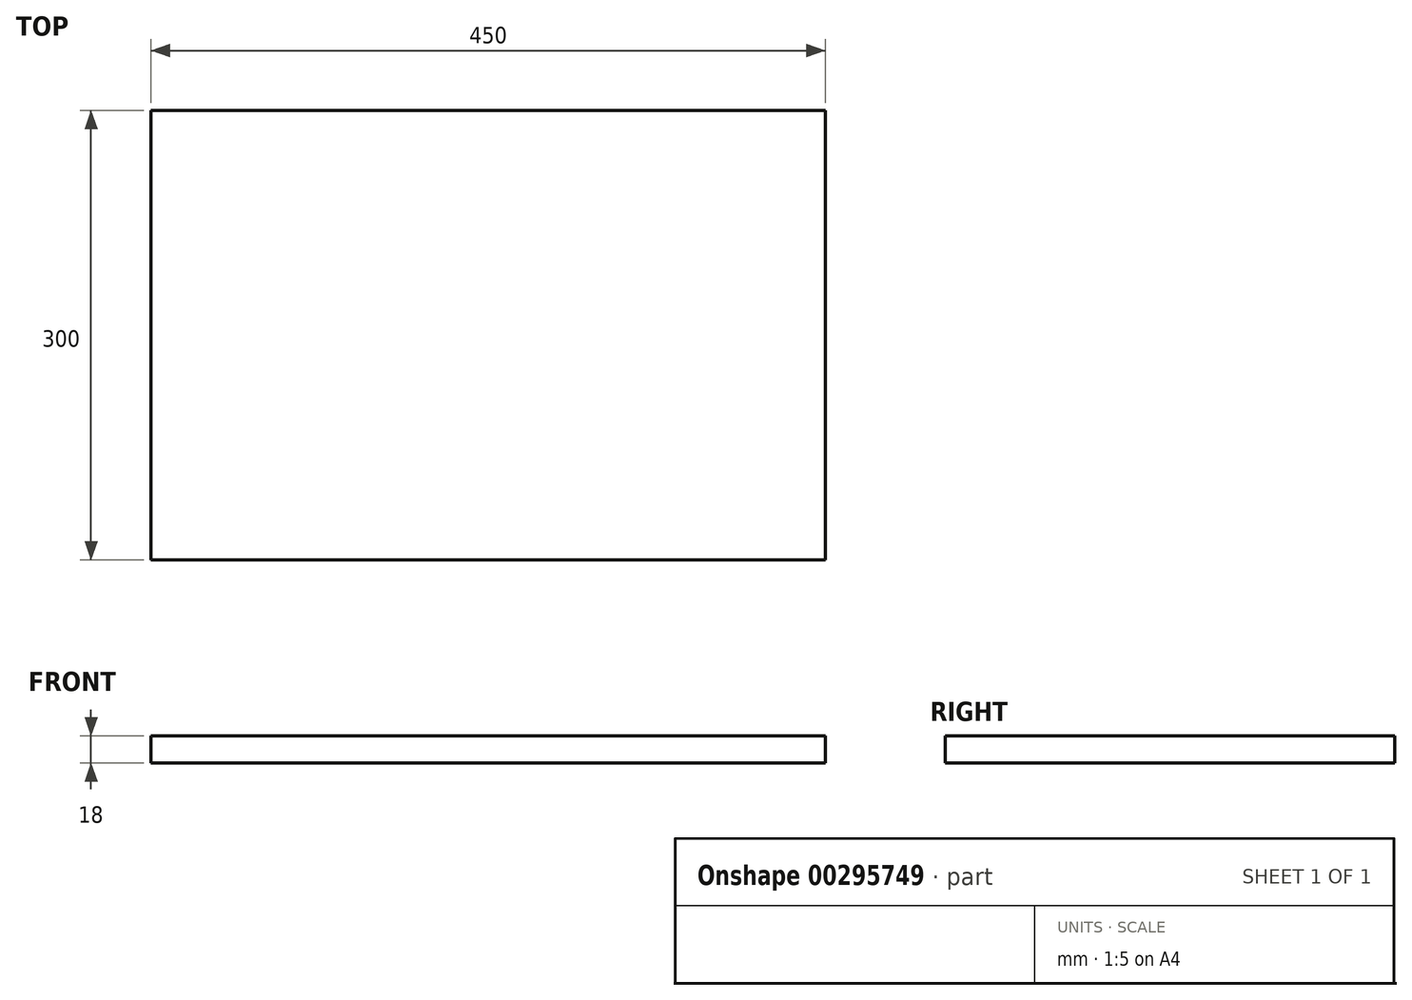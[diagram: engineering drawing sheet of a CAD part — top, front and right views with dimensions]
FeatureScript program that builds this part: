
annotation { "Feature Type Name" : "Feature", "Feature Type Description" : "" }
export const myFeature = defineFeature(function(context is Context, id is Id, definition is map)
    precondition{}
    {
        {
            var Q0;
            Q0=qCreatedBy(makeId("Top.planeOp"),FACE);
            var sketch = newSketch(context, id + "F0", { "sketchPlane" : qUnion([Q0])});
            skLineSegment(sketch, "E0.bottom", {"start": v(-247.7, 149.01) * mm, "end": v(202.3, 149.01) * mm});
            skLineSegment(sketch, "E0.top", {"start": v(-247.7, -150.99) * mm, "end": v(202.3, -150.99) * mm});
            skLineSegment(sketch, "E0.left", {"start": v(-247.7, 149.01) * mm, "end": v(-247.7, -150.99) * mm});
            skLineSegment(sketch, "E0.right", {"start": v(202.3, 149.01) * mm, "end": v(202.3, -150.99) * mm});
            skSolve(sketch);
        }
        {
            var Q0;
            Q0=makeQuery(id+"F0.imprint","IMPRINT",FACE,{"disambiguationData":[TD([[makeQuery(id+"F0.imprint","IMPRINT",EDGE,{"derivedFrom":sQuery(id+"F0.wireOp",EDGE,"E0.bottom")}),-1.0]])]});
            extrude(context, id + "F1", {"entities" : qUnion([Q0]), "depth" : 18 * mm});
        }
    });
